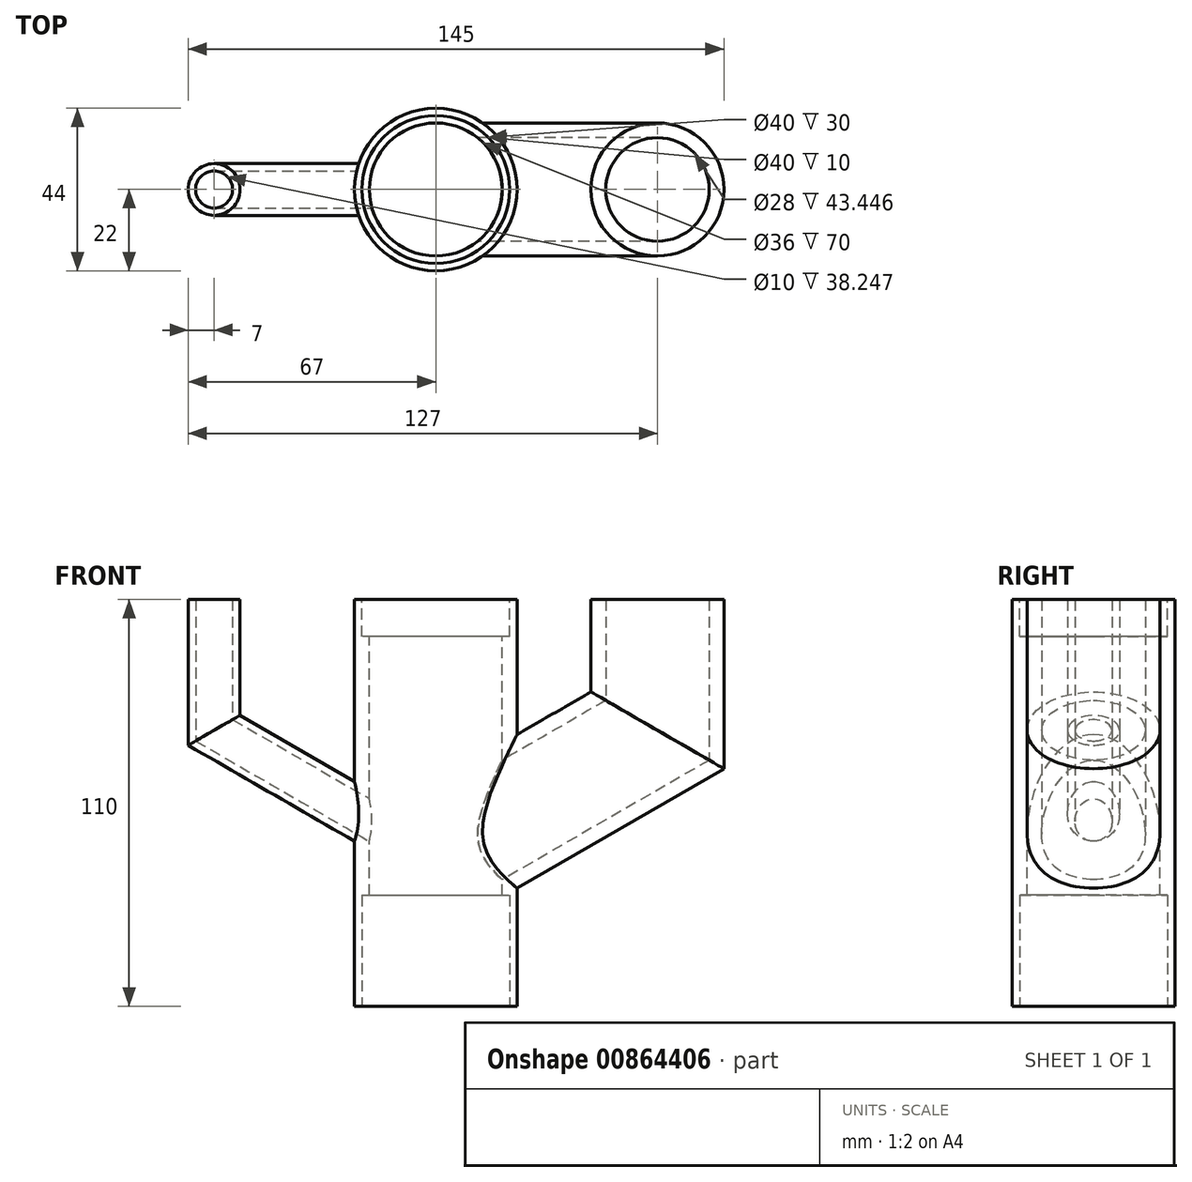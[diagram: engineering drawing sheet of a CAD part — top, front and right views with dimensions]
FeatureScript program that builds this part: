
annotation { "Feature Type Name" : "Feature", "Feature Type Description" : "" }
export const myFeature = defineFeature(function(context is Context, id is Id, definition is map)
    precondition{}
    {
        {
            var Q0;
            Q0=qCreatedBy(makeId("Front.planeOp"),FACE);
            var sketch = newSketch(context, id + "F0", { "sketchPlane" : qUnion([Q0])});
            skLineSegment(sketch, "E0", {"start": v(0, 0) * mm, "end": v(0, -70) * mm});
            skLineSegment(sketch, "E1", {"start": v(0, -70) * mm, "end": v(60, -35.36) * mm});
            skLineSegment(sketch, "E2", {"start": v(60, -35.36) * mm, "end": v(60, 0) * mm});
            skLineSegment(sketch, "E3", {"start": v(0, -70) * mm, "end": v(0, -110) * mm});
            skLineSegment(sketch, "E4", {"start": v(0, 0) * mm, "end": v(0, -35.36) * mm});
            skLineSegment(sketch, "E5", {"start": v(0, -35.36) * mm, "end": v(0, -70) * mm});
            skLineSegment(sketch, "E6", {"start": v(0, -70) * mm, "end": v(-60, -35.36) * mm});
            skLineSegment(sketch, "E7", {"start": v(-60, -35.36) * mm, "end": v(-60, 0) * mm});
            skSolve(sketch);
        }
        {
            var Q0;
            Q0=qCreatedBy(makeId("Top.planeOp"),FACE);
            var sketch = newSketch(context, id + "F1", { "sketchPlane" : qUnion([Q0])});
            skCircle(sketch, "E8", {"center": v(0, 0) * mm, "radius": 22 * mm});
            skCircle(sketch, "E9", {"center": v(60, 0) * mm, "radius": 18 * mm});
            skCircle(sketch, "E10", {"center": v(-60, 0) * mm, "radius": 7 * mm});
            skSolve(sketch);
        }
        {
            var Q0;
            Q0=makeQuery(id+"F1.imprint","IMPRINT",FACE,{"disambiguationData":[TD([[makeQuery(id+"F1.imprint","IMPRINT",EDGE,{"derivedFrom":sQuery(id+"F1.wireOp",EDGE,"E8")}),1.0]])]});
            var Q1;
            Q1=sQuery(id+"F0.wireOp",EDGE,"E0");
            var Q2;
            Q2=sQuery(id+"F0.wireOp",EDGE,"E3");
            sweep(context, id + "F2", {"profiles" : qUnion([Q0]), "path" : qUnion([Q1, Q2])});
        }
        {
            var Q0;
            Q0=makeQuery(id+"F1.imprint","IMPRINT",FACE,{"disambiguationData":[TD([[makeQuery(id+"F1.imprint","IMPRINT",EDGE,{"derivedFrom":sQuery(id+"F1.wireOp",EDGE,"E9")}),1.0]])]});
            var Q1;
            Q1=sQuery(id+"F0.wireOp",EDGE,"E2");
            var Q2;
            Q2=sQuery(id+"F0.wireOp",EDGE,"E1");
            sweep(context, id + "F3", {"operationType" : NewBodyOperationType.ADD, "profiles" : qUnion([Q0]), "path" : qUnion([Q1, Q2])});
        }
        {
            var Q0;
            Q0=makeQuery(id+"F2.opSweep","CAP_FACE",FACE,{"disambiguationData":[OSD([sQuery(id+"F0.wireOp",VERTEX,"E3.end"),sQuery(id+"F1.wireOp",EDGE,"E8")])],"isStart":false});
            var sketch = newSketch(context, id + "F4", { "sketchPlane" : qUnion([Q0])});
            skCircle(sketch, "E11", {"center": v(0, 0) * mm, "radius": 20 * mm});
            skSolve(sketch);
        }
        {
            var Q0;
            Q0 = qSketchRegion(id + "F4", true);
            extrude(context, id + "F5", {"entities" : qUnion([Q0]), "operationType" : NewBodyOperationType.REMOVE, "oppositeDirection" : true, "depth" : 30 * mm, "offsetDistance" : 25 * mm});
        }
        {
            var Q0;
            Q0=makeQuery(id+"F1.imprint","IMPRINT",FACE,{"disambiguationData":[TD([[makeQuery(id+"F1.imprint","IMPRINT",EDGE,{"derivedFrom":sQuery(id+"F1.wireOp",EDGE,"E8")}),1.0]])]});
            var sketch = newSketch(context, id + "F6", { "sketchPlane" : qUnion([Q0])});
            skCircle(sketch, "E12", {"center": v(0, 0) * mm, "radius": 18 * mm});
            skSolve(sketch);
        }
        {
            var Q0;
            Q0=makeQuery(id+"F1.imprint","IMPRINT",FACE,{"disambiguationData":[TD([[makeQuery(id+"F1.imprint","IMPRINT",EDGE,{"derivedFrom":sQuery(id+"F1.wireOp",EDGE,"E8")}),1.0]])]});
            var sketch = newSketch(context, id + "F7", { "sketchPlane" : qUnion([Q0])});
            skCircle(sketch, "E13", {"center": v(0, 0) * mm, "radius": 18 * mm});
            skCircle(sketch, "E14", {"center": v(0, 0) * mm, "radius": 20 * mm});
            skSolve(sketch);
        }
        {
            var Q0;
            Q0=makeQuery(id+"F7.imprint","IMPRINT",FACE,{"disambiguationData":[TD([[makeQuery(id+"F7.imprint","IMPRINT",EDGE,{"derivedFrom":sQuery(id+"F7.wireOp",EDGE,"E13")}),-1.0]])]});
            extrude(context, id + "F8", {"entities" : qUnion([Q0]), "operationType" : NewBodyOperationType.REMOVE, "oppositeDirection" : true, "depth" : 10 * mm, "offsetDistance" : 25 * mm});
        }
        {
            var Q0;
            Q0=makeQuery(id+"F1.imprint","IMPRINT",FACE,{"disambiguationData":[TD([[makeQuery(id+"F1.imprint","IMPRINT",EDGE,{"derivedFrom":sQuery(id+"F1.wireOp",EDGE,"E9")}),1.0]])]});
            var sketch = newSketch(context, id + "F9", { "sketchPlane" : qUnion([Q0])});
            skCircle(sketch, "E15", {"center": v(60, 0) * mm, "radius": 14 * mm});
            skSolve(sketch);
        }
        {
            var Q0;
            Q0=makeQuery(id+"F9.imprint","IMPRINT",FACE,{"disambiguationData":[TD([[makeQuery(id+"F9.imprint","IMPRINT",EDGE,{"derivedFrom":sQuery(id+"F9.wireOp",EDGE,"E15")}),1.0]])]});
            var Q1;
            Q1=sQuery(id+"F0.wireOp",EDGE,"E2");
            var Q2;
            Q2=sQuery(id+"F0.wireOp",EDGE,"E1");
            sweep(context, id + "F10", {"operationType" : NewBodyOperationType.REMOVE, "profiles" : qUnion([Q0]), "path" : qUnion([Q1, Q2])});
        }
        {
            var Q0;
            Q0=makeQuery(id+"F1.imprint","IMPRINT",FACE,{"disambiguationData":[TD([[makeQuery(id+"F1.imprint","IMPRINT",EDGE,{"derivedFrom":sQuery(id+"F1.wireOp",EDGE,"E10")}),1.0]])]});
            var Q1;
            Q1=sQuery(id+"F0.wireOp",EDGE,"E7");
            var Q2;
            Q2=sQuery(id+"F0.wireOp",EDGE,"E6");
            sweep(context, id + "F11", {"operationType" : NewBodyOperationType.ADD, "profiles" : qUnion([Q0]), "path" : qUnion([Q1, Q2])});
        }
        {
            var Q0;
            Q0 = qSketchRegion(id + "F6", true);
            extrude(context, id + "F12", {"entities" : qUnion([Q0]), "operationType" : NewBodyOperationType.REMOVE, "endBound" : BoundingType.THROUGH_ALL, "oppositeDirection" : true, "depth" : 25 * mm, "offsetDistance" : 25 * mm});
        }
        {
            var Q0;
            Q0=makeQuery(id+"F11.opSweep","CAP_FACE",FACE,{"disambiguationData":[OSD([sQuery(id+"F0.wireOp",VERTEX,"E7.end"),sQuery(id+"F1.wireOp",EDGE,"E10")])],"isStart":true});
            var sketch = newSketch(context, id + "F13", { "sketchPlane" : qUnion([Q0])});
            skCircle(sketch, "E16", {"center": v(-60, 0) * mm, "radius": 5 * mm});
            skSolve(sketch);
        }
        {
            var Q0;
            Q0 = qSketchRegion(id + "F13", true);
            var Q1;
            Q1=sQuery(id+"F0.wireOp",EDGE,"E7");
            var Q2;
            Q2=sQuery(id+"F0.wireOp",EDGE,"E6");
            sweep(context, id + "F14", {"operationType" : NewBodyOperationType.REMOVE, "profiles" : qUnion([Q0]), "path" : qUnion([Q1, Q2])});
        }
    });
